# Revit family: P3535.25
name_source: partatom
category: Luminarias
units: mm (PartAtom-declared; Revit-internal decimal feet)

## family parameters
Compartido = No
Corte con vacíos al cargar = No
Cota de conector redondo = Diámetro de uso
Origen de luz = No
Punto de cálculo de habitación = No
Se basa en plano de trabajo = Sí
Siempre vertical = No
Tipo de pieza = Normal

## types (1)
- P3535.25
    Comentarios de vataje = 24V
    Costo = 0 $
    Descripción = PERFIL DE ALUMINIO PARA SUSPENDER, EMPOTRAR Y SOBREPONER DE 2.5M DE PERFIL CON UN MATERIAL DE ALUMINIO ANODIZADO Y DIMENSIONES DE 35X35MM PESO DE 1.99KG POR PERFIL, TABLILLA LED CON UNA POTENCIA DE 10.6W, TEMPERATURA DE COLOR A BLANCO CALIDO 3000K, TABLILLA DE 499MM CORTE A CADA 100MM/14 LEDs, 1060lm/pcs, IRC 80, ALIMENTADO A 24V. REQUIERE ACCESORIOS.
    Elevación por defecto = 0 mm  [stored 0 ft]
    Fabricante = BRILLANT
    Lámpara = Tablilla
    Modelo = P3535.25

note: [stored X ft] marks values corroborated as IEEE doubles in the binary element streams (Revit-internal decimal feet)

## geometry (parser evidence)
native form markers: Blend x2
no freeform markers — native parametric forms only
